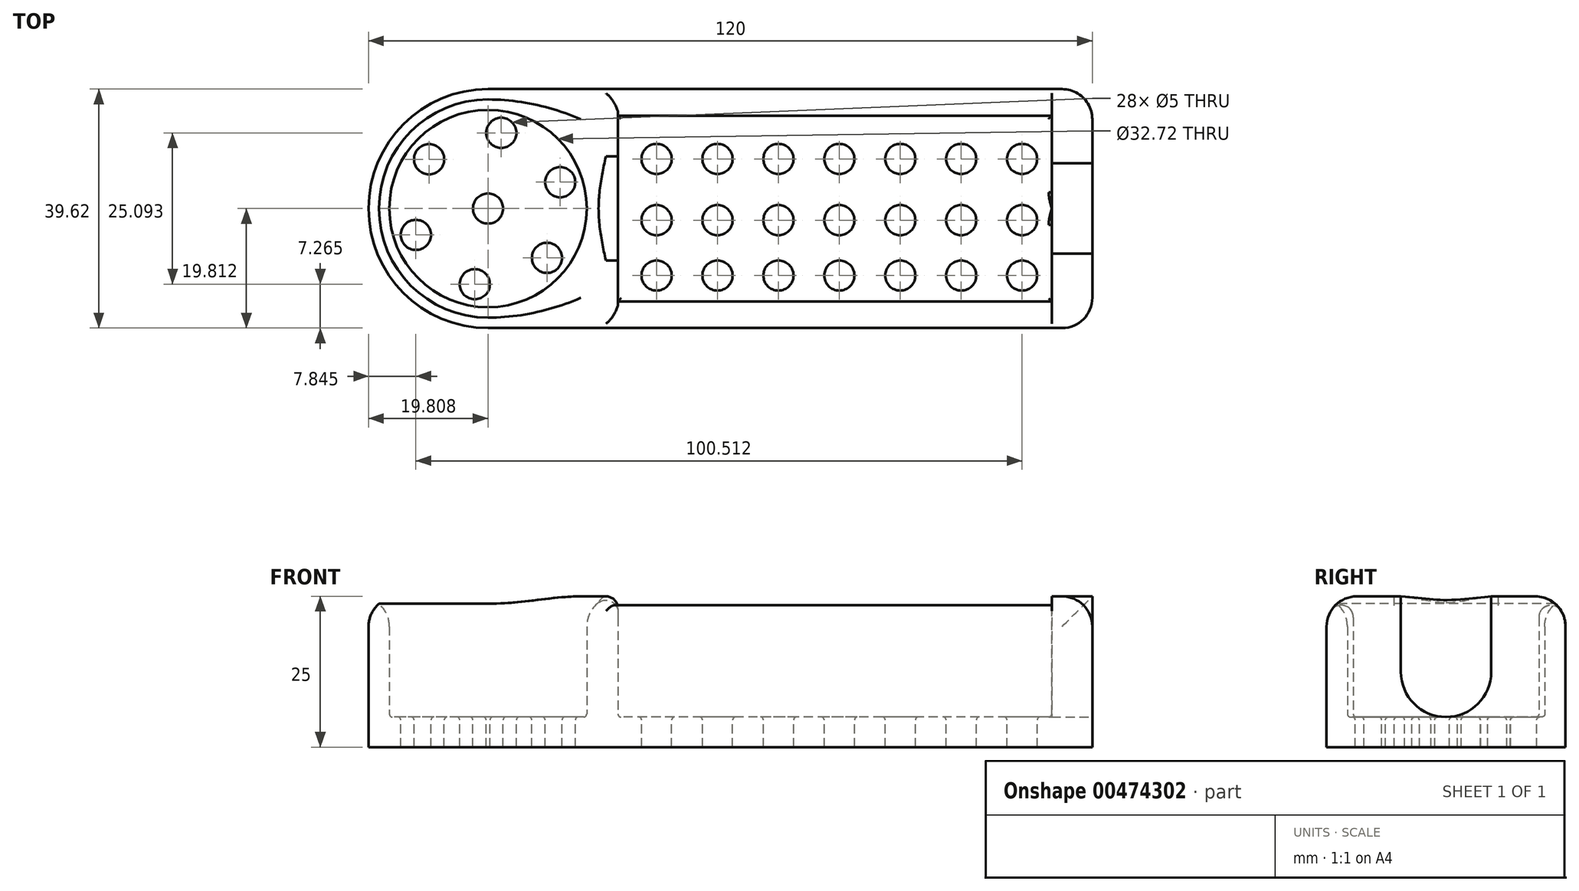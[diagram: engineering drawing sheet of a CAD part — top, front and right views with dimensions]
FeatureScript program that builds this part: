
annotation { "Feature Type Name" : "Feature", "Feature Type Description" : "" }
export const myFeature = defineFeature(function(context is Context, id is Id, definition is map)
    precondition{}
    {
        {
            var Q0;
            Q0=qCreatedBy(makeId("Top.planeOp"),FACE);
            var sketch = newSketch(context, id + "F0", { "sketchPlane" : qUnion([Q0])});
            skCircle(sketch, "E0", {"center": v(-57.21, 24.71) * mm, "radius": 19.8 * mm});
            skLineSegment(sketch, "E1", {"start": v(-57.21, 44.52) * mm, "end": v(42.98, 44.52) * mm});
            skLineSegment(sketch, "E2", {"start": v(42.98, 44.52) * mm, "end": v(42.98, 4.9) * mm});
            skLineSegment(sketch, "E3", {"start": v(42.98, 4.9) * mm, "end": v(-57.21, 4.9) * mm});
            skCircle(sketch, "E4", {"center": v(-57.21, 24.71) * mm, "radius": 16.36 * mm});
            skLineSegment(sketch, "E5.bottom", {"start": v(-35.67, 40.1) * mm, "end": v(36.25, 40.1) * mm});
            skLineSegment(sketch, "E5.top", {"start": v(-35.67, 9.33) * mm, "end": v(36.25, 9.33) * mm});
            skLineSegment(sketch, "E5.left", {"start": v(-35.67, 40.1) * mm, "end": v(-35.67, 9.33) * mm});
            skLineSegment(sketch, "E5.right", {"start": v(36.25, 40.1) * mm, "end": v(36.25, 9.33) * mm});
            skLineSegment(sketch, "E6", {"start": v(-35.67, 9.33) * mm, "end": v(-35.67, 4.9) * mm});
            skLineSegment(sketch, "E7", {"start": v(-35.67, 40.1) * mm, "end": v(-35.67, 44.52) * mm});
            skSolve(sketch);
        }
        {
            var Q0;
            Q0=makeQuery(id+"F0.imprint","IMPRINT",FACE,{"disambiguationData":[TD([[makeQuery(id+"F0.imprint","IMPRINT",EDGE,{"derivedFrom":sQuery(id+"F0.wireOp",EDGE,"E4")}),-1.0]])]});
            var Q1;
            Q1=makeQuery(id+"F0.imprint","IMPRINT",FACE,{"disambiguationData":[TD([[makeQuery(id+"F0.imprint","IMPRINT",EDGE,{"derivedFrom":sQuery(id+"F0.wireOp",EDGE,"E4")}),1.0]])]});
            var Q2;
            Q2=makeQuery(id+"F0.imprint","IMPRINT",FACE,{"disambiguationData":[TD([[makeQuery(id+"F0.imprint","IMPRINT",EDGE,{"derivedFrom":sQuery(id+"F0.wireOp",EDGE,"E5.left")}),-1.0]])]});
            var Q3;
            {var subQ1=sQuery(id+"F0.wireOp",EDGE,"E2");Q3=makeQuery(id+"F0.imprint","IMPRINT",FACE,{"disambiguationData":[TD([[makeQuery(id+"F0.imprint","IMPRINT",EDGE,{"derivedFrom":subQ1}),-1.0]])]});}
            var Q4;
            Q4=makeQuery(id+"F0.imprint","IMPRINT",FACE,{"disambiguationData":[TD([[makeQuery(id+"F0.imprint","IMPRINT",EDGE,{"derivedFrom":sQuery(id+"F0.wireOp",EDGE,"E5.bottom")}),-1.0]])]});
            extrude(context, id + "F1", {"entities" : qUnion([Q0, Q1, Q2, Q3, Q4]), "depth" : 5 * mm});
        }
        {
            var Q0;
            Q0=makeQuery(id+"F0.imprint","IMPRINT",FACE,{"disambiguationData":[TD([[makeQuery(id+"F0.imprint","IMPRINT",EDGE,{"derivedFrom":sQuery(id+"F0.wireOp",EDGE,"E4")}),-1.0]])]});
            var Q1;
            {var subQ1=sQuery(id+"F0.wireOp",EDGE,"E2");Q1=makeQuery(id+"F0.imprint","IMPRINT",FACE,{"disambiguationData":[TD([[makeQuery(id+"F0.imprint","IMPRINT",EDGE,{"derivedFrom":subQ1}),-1.0]])]});}
            var Q2;
            Q2=makeQuery(id+"F0.imprint","IMPRINT",FACE,{"disambiguationData":[TD([[makeQuery(id+"F0.imprint","IMPRINT",EDGE,{"derivedFrom":sQuery(id+"F0.wireOp",EDGE,"E5.left")}),-1.0]])]});
            extrude(context, id + "F2", {"entities" : qUnion([Q0, Q1, Q2]), "operationType" : NewBodyOperationType.ADD, "depth" : 25 * mm});
        }
        {
            var Q0;
            {var subQ0=sQuery(id+"F0.wireOp",EDGE,"E2");Q0=makeQuery(id+"F2.boolean.opBoolean","MERGE",FACE,{"derivedFrom":[makeQuery(id+"F1.opExtrude","SWEPT_FACE",FACE,{"disambiguationData":[OSD([subQ0])]}),makeQuery(id+"F2.opExtrude","SWEPT_FACE",FACE,{"disambiguationData":[OSD([subQ0])]})]});}
            var sketch = newSketch(context, id + "F3", { "sketchPlane" : qUnion([Q0])});
            skArc(sketch, "E8", {"start": v(17.21, 12.5) * mm, "mid": v(24.71, 5) * mm, "end": v(32.21, 12.5) * mm});
            skPoint(sketch, "E9.start.orphan", {"position": v(24.71, 25) * mm});
            skLineSegment(sketch, "E10", {"start": v(32.21, 12.5) * mm, "end": v(32.21, 25) * mm});
            skLineSegment(sketch, "E11", {"start": v(17.21, 12.5) * mm, "end": v(17.21, 25) * mm});
            skPoint(sketch, "E12.trimOffspring.end.orphan", {"position": v(24.71, 0) * mm});
            skSolve(sketch);
        }
        {
            var Q0;
            Q0=makeQuery(id+"F3.imprint","IMPRINT",FACE,{"disambiguationData":[TD([[makeQuery(id+"F3.imprint","IMPRINT",EDGE,{"derivedFrom":sQuery(id+"F3.wireOp",EDGE,"E8")}),1.0]])]});
            extrude(context, id + "F4", {"entities" : qUnion([Q0]), "operationType" : NewBodyOperationType.REMOVE, "oppositeDirection" : true, "depth" : 25 * mm});
        }
        {
            var Q0;
            Q0=makeQuery(id+"F4.boolean.opBoolean","COPY",EDGE,{"derivedFrom":makeQuery(id+"F4.opExtrude","SWEPT_EDGE",EDGE,{"disambiguationData":[OSD([sQuery(id+"F0.wireOp",EDGE,"E2"),sQuery(id+"F3.wireOp",EDGE,"E11")])]})});
            var Q1;
            Q1=makeQuery(id+"F4.boolean.opBoolean","COPY",EDGE,{"derivedFrom":makeQuery(id+"F4.opExtrude","SWEPT_EDGE",EDGE,{"disambiguationData":[OSD([sQuery(id+"F0.wireOp",EDGE,"E2"),sQuery(id+"F3.wireOp",EDGE,"E10")])]})});
            var Q2;
            Q2=makeQuery(id+"F4.boolean.opBoolean","COPY",EDGE,{"derivedFrom":makeQuery(id+"F4.opExtrude","CAP_EDGE",EDGE,{"disambiguationData":[OSD([sQuery(id+"F3.wireOp",EDGE,"E11")])],"isStart":true})});
            var Q3;
            {var subQ0=sQuery(id+"F0.wireOp",EDGE,"E3");var subQ1=sQuery(id+"F0.wireOp",EDGE,"E2");Q3=makeQuery(id+"F4.boolean.opBoolean","SPLIT",EDGE,{"disambiguationData":[TD([makeQuery(id+"F1.opExtrude","SWEPT_FACE",FACE,{"disambiguationData":[OSD([subQ0])]})])],"derivedFrom":makeQuery(id+"F2.opExtrude","CAP_EDGE",EDGE,{"disambiguationData":[OSD([subQ1])],"isStart":false})});}
            var Q4;
            Q4=makeQuery(id+"F2.opExtrude","CAP_EDGE",EDGE,{"disambiguationData":[OSD([sQuery(id+"F0.wireOp",EDGE,"E3")])],"isStart":false});
            var Q5;
            {var subQ0=sQuery(id+"F0.wireOp",EDGE,"E2");var subQ1=sQuery(id+"F0.wireOp",EDGE,"E1");Q5=makeQuery(id+"F2.boolean.opBoolean","MERGE",EDGE,{"derivedFrom":[makeQuery(id+"F1.opExtrude","SWEPT_EDGE",EDGE,{"disambiguationData":[OSD([subQ1,subQ0])]}),makeQuery(id+"F2.opExtrude","SWEPT_EDGE",EDGE,{"disambiguationData":[OSD([subQ1,subQ0])]})]});}
            var Q6;
            {var subQ0=sQuery(id+"F0.wireOp",EDGE,"E3");var subQ1=sQuery(id+"F0.wireOp",EDGE,"E2");Q6=makeQuery(id+"F2.boolean.opBoolean","MERGE",EDGE,{"derivedFrom":[makeQuery(id+"F1.opExtrude","SWEPT_EDGE",EDGE,{"disambiguationData":[OSD([subQ1,subQ0])]}),makeQuery(id+"F2.opExtrude","SWEPT_EDGE",EDGE,{"disambiguationData":[OSD([subQ1,subQ0])]})]});}
            var Q7;
            Q7=makeQuery(id+"F2.opExtrude","CAP_EDGE",EDGE,{"disambiguationData":[OSD([sQuery(id+"F0.wireOp",EDGE,"E4")])],"isStart":false});
            fillet(context, id + "F5", {"entities" : qUnion([Q0, Q1, Q2, Q3, Q4, Q5, Q6, Q7]), "radius" : 5 * mm, "tangentPropagation" : true, "allowEdgeOverflow" : false});
        }
        {
            var Q0;
            Q0=makeQuery(id+"F2.opExtrude","CAP_EDGE",EDGE,{"disambiguationData":[OSD([sQuery(id+"F0.wireOp",EDGE,"E5.left")])],"isStart":false});
            var Q1;
            Q1=makeQuery(id+"F5.opFillet","BLEND_EDGE",EDGE,{"blendedFrom":[makeQuery(id+"F2.opExtrude","CAP_EDGE",EDGE,{"disambiguationData":[OSD([sQuery(id+"F0.wireOp",EDGE,"E3")])],"isStart":false}),makeQuery(id+"F2.opExtrude","SWEPT_FACE",FACE,{"disambiguationData":[OSD([sQuery(id+"F0.wireOp",EDGE,"E5.top")])]})],"blendedInto":[makeQuery(id+"F2.opExtrude","SWEPT_FACE",FACE,{"disambiguationData":[OSD([sQuery(id+"F0.wireOp",EDGE,"E5.top")])]})]});
            var Q2;
            Q2=makeQuery(id+"F5.opFillet","BLEND_EDGE",EDGE,{"blendedFrom":[makeQuery(id+"F2.opExtrude","CAP_EDGE",EDGE,{"disambiguationData":[OSD([sQuery(id+"F0.wireOp",EDGE,"E1")])],"isStart":false}),makeQuery(id+"F2.opExtrude","SWEPT_FACE",FACE,{"disambiguationData":[OSD([sQuery(id+"F0.wireOp",EDGE,"E5.bottom")])]})],"blendedInto":[makeQuery(id+"F2.opExtrude","SWEPT_FACE",FACE,{"disambiguationData":[OSD([sQuery(id+"F0.wireOp",EDGE,"E5.bottom")])]})]});
            var Q3;
            {var subQ0=sQuery(id+"F0.wireOp",EDGE,"E5.right");var subQ1=makeQuery(id+"F2.opExtrude","SWEPT_FACE",FACE,{"disambiguationData":[OSD([subQ0])]});var subQ2=sQuery(id+"F0.wireOp",EDGE,"E5.bottom");var subQ4=sQuery(id+"F0.wireOp",EDGE,"E2");var subQ7=sQuery(id+"F3.wireOp",EDGE,"E10");Q3=makeQuery(id+"F5.opFillet","BLEND_EDGE",EDGE,{"blendedFrom":[makeQuery(id+"F4.boolean.opBoolean","COPY",EDGE,{"derivedFrom":makeQuery(id+"F4.opExtrude","SWEPT_EDGE",EDGE,{"disambiguationData":[OSD([subQ4,subQ7])]})}),makeQuery(id+"F4.boolean.opBoolean","SPLIT",FACE,{"disambiguationData":[TD([makeQuery(id+"F2.opExtrude","SWEPT_FACE",FACE,{"disambiguationData":[OSD([subQ2])]})])],"derivedFrom":subQ1})],"blendedInto":[makeQuery(id+"F4.boolean.opBoolean","SPLIT",FACE,{"disambiguationData":[TD([makeQuery(id+"F2.opExtrude","SWEPT_FACE",FACE,{"disambiguationData":[OSD([subQ2])]})])],"derivedFrom":subQ1})]});}
            fillet(context, id + "F6", {"entities" : qUnion([Q0, Q1, Q2, Q3]), "radius" : 2 * mm, "tangentPropagation" : true, "allowEdgeOverflow" : false});
        }
        {
            var Q0;
            Q0=makeQuery(id+"F2.boolean.opBoolean","SPLIT",FACE,{"disambiguationData":[TD([makeQuery(id+"F2.opExtrude","SWEPT_FACE",FACE,{"disambiguationData":[OSD([sQuery(id+"F0.wireOp",EDGE,"E5.bottom")])]})])],"derivedFrom":makeQuery(id+"F1.opExtrude","CAP_FACE",FACE,{"disambiguationData":[OSD([sQuery(id+"F0.wireOp",EDGE,"E0"),sQuery(id+"F0.wireOp",EDGE,"E1"),sQuery(id+"F0.wireOp",EDGE,"E2"),sQuery(id+"F0.wireOp",EDGE,"E3")])],"isStart":false})});
            var sketch = newSketch(context, id + "F7", { "sketchPlane" : qUnion([Q0])});
            skCircle(sketch, "E13", {"center": v(-29.26, 32.94) * mm, "radius": 2.5 * mm});
            skCircle(sketch, "E14.1.0.0", {"center": v(-19.16, 32.94) * mm, "radius": 2.5 * mm});
            skCircle(sketch, "E14.2.0.0", {"center": v(-9.06, 32.94) * mm, "radius": 2.5 * mm});
            skCircle(sketch, "E14.3.0.0", {"center": v(1.04, 32.94) * mm, "radius": 2.5 * mm});
            skCircle(sketch, "E14.4.0.0", {"center": v(11.14, 32.94) * mm, "radius": 2.5 * mm});
            skCircle(sketch, "E14.5.0.0", {"center": v(21.24, 32.94) * mm, "radius": 2.5 * mm});
            skCircle(sketch, "E14.6.0.0", {"center": v(31.34, 32.94) * mm, "radius": 2.5 * mm});
            skLineSegment(sketch, "E14.direction1", {"start": v(-29.26, 32.94) * mm, "end": v(-19.16, 32.94) * mm, "construction": true});
            skCircle(sketch, "E15", {"center": v(-29.26, 22.78) * mm, "radius": 2.5 * mm});
            skCircle(sketch, "E16.1.0.0", {"center": v(-19.16, 22.78) * mm, "radius": 2.5 * mm});
            skCircle(sketch, "E16.2.0.0", {"center": v(-9.06, 22.78) * mm, "radius": 2.5 * mm});
            skCircle(sketch, "E16.3.0.0", {"center": v(1.04, 22.78) * mm, "radius": 2.5 * mm});
            skCircle(sketch, "E16.4.0.0", {"center": v(11.14, 22.78) * mm, "radius": 2.5 * mm});
            skCircle(sketch, "E16.5.0.0", {"center": v(21.24, 22.78) * mm, "radius": 2.5 * mm});
            skCircle(sketch, "E16.6.0.0", {"center": v(31.34, 22.78) * mm, "radius": 2.5 * mm});
            skLineSegment(sketch, "E16.direction1", {"start": v(-29.26, 22.78) * mm, "end": v(-19.16, 22.78) * mm, "construction": true});
            skCircle(sketch, "E17", {"center": v(-29.26, 13.6) * mm, "radius": 2.5 * mm});
            skCircle(sketch, "E18.1.0.0", {"center": v(-19.16, 13.6) * mm, "radius": 2.5 * mm});
            skCircle(sketch, "E18.2.0.0", {"center": v(-9.06, 13.6) * mm, "radius": 2.5 * mm});
            skCircle(sketch, "E18.3.0.0", {"center": v(1.04, 13.6) * mm, "radius": 2.5 * mm});
            skCircle(sketch, "E18.4.0.0", {"center": v(11.14, 13.6) * mm, "radius": 2.5 * mm});
            skCircle(sketch, "E18.5.0.0", {"center": v(21.24, 13.6) * mm, "radius": 2.5 * mm});
            skCircle(sketch, "E18.6.0.0", {"center": v(31.34, 13.6) * mm, "radius": 2.5 * mm});
            skLineSegment(sketch, "E18.direction1", {"start": v(-29.26, 13.6) * mm, "end": v(-19.16, 13.6) * mm, "construction": true});
            skSolve(sketch);
        }
        {
            var Q0;
            Q0=makeQuery(id+"F7.imprint","IMPRINT",FACE,{"disambiguationData":[TD([[makeQuery(id+"F7.imprint","IMPRINT",EDGE,{"derivedFrom":sQuery(id+"F7.wireOp",EDGE,"E13")}),1.0]])]});
            var Q1;
            Q1=makeQuery(id+"F7.imprint","IMPRINT",FACE,{"disambiguationData":[TD([[makeQuery(id+"F7.imprint","IMPRINT",EDGE,{"derivedFrom":sQuery(id+"F7.wireOp",EDGE,"E14.1.0.0")}),1.0]])]});
            var Q2;
            Q2=makeQuery(id+"F7.imprint","IMPRINT",FACE,{"disambiguationData":[TD([[makeQuery(id+"F7.imprint","IMPRINT",EDGE,{"derivedFrom":sQuery(id+"F7.wireOp",EDGE,"E14.2.0.0")}),1.0]])]});
            var Q3;
            Q3=makeQuery(id+"F7.imprint","IMPRINT",FACE,{"disambiguationData":[TD([[makeQuery(id+"F7.imprint","IMPRINT",EDGE,{"derivedFrom":sQuery(id+"F7.wireOp",EDGE,"E14.3.0.0")}),1.0]])]});
            var Q4;
            Q4=makeQuery(id+"F7.imprint","IMPRINT",FACE,{"disambiguationData":[TD([[makeQuery(id+"F7.imprint","IMPRINT",EDGE,{"derivedFrom":sQuery(id+"F7.wireOp",EDGE,"E14.4.0.0")}),1.0]])]});
            var Q5;
            Q5=makeQuery(id+"F7.imprint","IMPRINT",FACE,{"disambiguationData":[TD([[makeQuery(id+"F7.imprint","IMPRINT",EDGE,{"derivedFrom":sQuery(id+"F7.wireOp",EDGE,"E14.5.0.0")}),1.0]])]});
            var Q6;
            Q6=makeQuery(id+"F7.imprint","IMPRINT",FACE,{"disambiguationData":[TD([[makeQuery(id+"F7.imprint","IMPRINT",EDGE,{"derivedFrom":sQuery(id+"F7.wireOp",EDGE,"E14.6.0.0")}),1.0]])]});
            var Q7;
            Q7=makeQuery(id+"F7.imprint","IMPRINT",FACE,{"disambiguationData":[TD([[makeQuery(id+"F7.imprint","IMPRINT",EDGE,{"derivedFrom":sQuery(id+"F7.wireOp",EDGE,"E16.6.0.0")}),1.0]])]});
            var Q8;
            Q8=makeQuery(id+"F7.imprint","IMPRINT",FACE,{"disambiguationData":[TD([[makeQuery(id+"F7.imprint","IMPRINT",EDGE,{"derivedFrom":sQuery(id+"F7.wireOp",EDGE,"E18.6.0.0")}),1.0]])]});
            var Q9;
            Q9=makeQuery(id+"F7.imprint","IMPRINT",FACE,{"disambiguationData":[TD([[makeQuery(id+"F7.imprint","IMPRINT",EDGE,{"derivedFrom":sQuery(id+"F7.wireOp",EDGE,"E18.5.0.0")}),1.0]])]});
            var Q10;
            Q10=makeQuery(id+"F7.imprint","IMPRINT",FACE,{"disambiguationData":[TD([[makeQuery(id+"F7.imprint","IMPRINT",EDGE,{"derivedFrom":sQuery(id+"F7.wireOp",EDGE,"E16.5.0.0")}),1.0]])]});
            var Q11;
            Q11=makeQuery(id+"F7.imprint","IMPRINT",FACE,{"disambiguationData":[TD([[makeQuery(id+"F7.imprint","IMPRINT",EDGE,{"derivedFrom":sQuery(id+"F7.wireOp",EDGE,"E16.4.0.0")}),1.0]])]});
            var Q12;
            Q12=makeQuery(id+"F7.imprint","IMPRINT",FACE,{"disambiguationData":[TD([[makeQuery(id+"F7.imprint","IMPRINT",EDGE,{"derivedFrom":sQuery(id+"F7.wireOp",EDGE,"E18.4.0.0")}),1.0]])]});
            var Q13;
            Q13=makeQuery(id+"F7.imprint","IMPRINT",FACE,{"disambiguationData":[TD([[makeQuery(id+"F7.imprint","IMPRINT",EDGE,{"derivedFrom":sQuery(id+"F7.wireOp",EDGE,"E18.3.0.0")}),1.0]])]});
            var Q14;
            Q14=makeQuery(id+"F7.imprint","IMPRINT",FACE,{"disambiguationData":[TD([[makeQuery(id+"F7.imprint","IMPRINT",EDGE,{"derivedFrom":sQuery(id+"F7.wireOp",EDGE,"E16.3.0.0")}),1.0]])]});
            var Q15;
            Q15=makeQuery(id+"F7.imprint","IMPRINT",FACE,{"disambiguationData":[TD([[makeQuery(id+"F7.imprint","IMPRINT",EDGE,{"derivedFrom":sQuery(id+"F7.wireOp",EDGE,"E16.2.0.0")}),1.0]])]});
            var Q16;
            Q16=makeQuery(id+"F7.imprint","IMPRINT",FACE,{"disambiguationData":[TD([[makeQuery(id+"F7.imprint","IMPRINT",EDGE,{"derivedFrom":sQuery(id+"F7.wireOp",EDGE,"E18.2.0.0")}),1.0]])]});
            var Q17;
            Q17=makeQuery(id+"F7.imprint","IMPRINT",FACE,{"disambiguationData":[TD([[makeQuery(id+"F7.imprint","IMPRINT",EDGE,{"derivedFrom":sQuery(id+"F7.wireOp",EDGE,"E18.1.0.0")}),1.0]])]});
            var Q18;
            Q18=makeQuery(id+"F7.imprint","IMPRINT",FACE,{"disambiguationData":[TD([[makeQuery(id+"F7.imprint","IMPRINT",EDGE,{"derivedFrom":sQuery(id+"F7.wireOp",EDGE,"E16.1.0.0")}),1.0]])]});
            var Q19;
            Q19=makeQuery(id+"F7.imprint","IMPRINT",FACE,{"disambiguationData":[TD([[makeQuery(id+"F7.imprint","IMPRINT",EDGE,{"derivedFrom":sQuery(id+"F7.wireOp",EDGE,"E15")}),1.0]])]});
            var Q20;
            Q20=makeQuery(id+"F7.imprint","IMPRINT",FACE,{"disambiguationData":[TD([[makeQuery(id+"F7.imprint","IMPRINT",EDGE,{"derivedFrom":sQuery(id+"F7.wireOp",EDGE,"E17")}),1.0]])]});
            extrude(context, id + "F8", {"entities" : qUnion([Q0, Q1, Q2, Q3, Q4, Q5, Q6, Q7, Q8, Q9, Q10, Q11, Q12, Q13, Q14, Q15, Q16, Q17, Q18, Q19, Q20]), "operationType" : NewBodyOperationType.REMOVE, "oppositeDirection" : true, "depth" : 25 * mm});
        }
        {
            var Q0;
            Q0=makeQuery(id+"F2.boolean.opBoolean","SPLIT",FACE,{"disambiguationData":[TD([makeQuery(id+"F2.opExtrude","SWEPT_FACE",FACE,{"disambiguationData":[OSD([sQuery(id+"F0.wireOp",EDGE,"E4")])]})])],"derivedFrom":makeQuery(id+"F1.opExtrude","CAP_FACE",FACE,{"disambiguationData":[OSD([sQuery(id+"F0.wireOp",EDGE,"E0"),sQuery(id+"F0.wireOp",EDGE,"E1"),sQuery(id+"F0.wireOp",EDGE,"E2"),sQuery(id+"F0.wireOp",EDGE,"E3")])],"isStart":false})});
            var sketch = newSketch(context, id + "F9", { "sketchPlane" : qUnion([Q0])});
            skCircle(sketch, "E19", {"center": v(-55.02, 37.26) * mm, "radius": 2.5 * mm});
            skCircle(sketch, "E20.1.0", {"center": v(-66.98, 32.89) * mm, "radius": 2.5 * mm});
            skCircle(sketch, "E20.2.0", {"center": v(-69.17, 20.34) * mm, "radius": 2.5 * mm});
            skCircle(sketch, "E20.3.0", {"center": v(-59.4, 12.16) * mm, "radius": 2.5 * mm});
            skCircle(sketch, "E20.4.0", {"center": v(-47.44, 16.54) * mm, "radius": 2.5 * mm});
            skCircle(sketch, "E20.5.0", {"center": v(-45.25, 29.08) * mm, "radius": 2.5 * mm});
            skPoint(sketch, "E20.center", {"position": v(-57.21, 24.71) * mm});
            skCircle(sketch, "E21", {"center": v(-57.21, 24.71) * mm, "radius": 2.5 * mm});
            skSolve(sketch);
        }
        {
            var Q0;
            Q0=makeQuery(id+"F9.imprint","IMPRINT",FACE,{"disambiguationData":[TD([[makeQuery(id+"F9.imprint","IMPRINT",EDGE,{"derivedFrom":sQuery(id+"F9.wireOp",EDGE,"E19")}),1.0]])]});
            var Q1;
            Q1=makeQuery(id+"F9.imprint","IMPRINT",FACE,{"disambiguationData":[TD([[makeQuery(id+"F9.imprint","IMPRINT",EDGE,{"derivedFrom":sQuery(id+"F9.wireOp",EDGE,"E20.1.0")}),1.0]])]});
            var Q2;
            Q2=makeQuery(id+"F9.imprint","IMPRINT",FACE,{"disambiguationData":[TD([[makeQuery(id+"F9.imprint","IMPRINT",EDGE,{"derivedFrom":sQuery(id+"F9.wireOp",EDGE,"E21")}),1.0]])]});
            var Q3;
            Q3=makeQuery(id+"F9.imprint","IMPRINT",FACE,{"disambiguationData":[TD([[makeQuery(id+"F9.imprint","IMPRINT",EDGE,{"derivedFrom":sQuery(id+"F9.wireOp",EDGE,"E20.2.0")}),1.0]])]});
            var Q4;
            Q4=makeQuery(id+"F9.imprint","IMPRINT",FACE,{"disambiguationData":[TD([[makeQuery(id+"F9.imprint","IMPRINT",EDGE,{"derivedFrom":sQuery(id+"F9.wireOp",EDGE,"E20.3.0")}),1.0]])]});
            var Q5;
            Q5=makeQuery(id+"F9.imprint","IMPRINT",FACE,{"disambiguationData":[TD([[makeQuery(id+"F9.imprint","IMPRINT",EDGE,{"derivedFrom":sQuery(id+"F9.wireOp",EDGE,"E20.4.0")}),1.0]])]});
            var Q6;
            Q6=makeQuery(id+"F9.imprint","IMPRINT",FACE,{"disambiguationData":[TD([[makeQuery(id+"F9.imprint","IMPRINT",EDGE,{"derivedFrom":sQuery(id+"F9.wireOp",EDGE,"E20.5.0")}),1.0]])]});
            extrude(context, id + "F10", {"entities" : qUnion([Q0, Q1, Q2, Q3, Q4, Q5, Q6]), "operationType" : NewBodyOperationType.REMOVE, "oppositeDirection" : true, "depth" : 25 * mm});
        }
        {
            var Q0;
            Q0=makeQuery(id+"F8.boolean.opBoolean","COPY",EDGE,{"derivedFrom":makeQuery(id+"F8.opExtrude","CAP_EDGE",EDGE,{"disambiguationData":[OSD([sQuery(id+"F7.wireOp",EDGE,"E14.1.0.0")])],"isStart":true})});
            var Q1;
            Q1=makeQuery(id+"F8.boolean.opBoolean","COPY",EDGE,{"derivedFrom":makeQuery(id+"F8.opExtrude","CAP_EDGE",EDGE,{"disambiguationData":[OSD([sQuery(id+"F7.wireOp",EDGE,"E14.2.0.0")])],"isStart":true})});
            var Q2;
            Q2=makeQuery(id+"F2.boolean.opBoolean","SPLIT",FACE,{"disambiguationData":[TD([makeQuery(id+"F2.opExtrude","SWEPT_FACE",FACE,{"disambiguationData":[OSD([sQuery(id+"F0.wireOp",EDGE,"E5.bottom")])]})])],"derivedFrom":makeQuery(id+"F1.opExtrude","CAP_FACE",FACE,{"disambiguationData":[OSD([sQuery(id+"F0.wireOp",EDGE,"E0"),sQuery(id+"F0.wireOp",EDGE,"E1"),sQuery(id+"F0.wireOp",EDGE,"E2"),sQuery(id+"F0.wireOp",EDGE,"E3")])],"isStart":false})});
            fillet(context, id + "F11", {"entities" : qUnion([Q0, Q1, Q2]), "radius" : .5 * mm, "tangentPropagation" : true, "allowEdgeOverflow" : false});
        }
        {
            var Q0;
            Q0=makeQuery(id+"F2.boolean.opBoolean","SPLIT",FACE,{"disambiguationData":[TD([makeQuery(id+"F2.opExtrude","SWEPT_FACE",FACE,{"disambiguationData":[OSD([sQuery(id+"F0.wireOp",EDGE,"E4")])]})])],"derivedFrom":makeQuery(id+"F1.opExtrude","CAP_FACE",FACE,{"disambiguationData":[OSD([sQuery(id+"F0.wireOp",EDGE,"E0"),sQuery(id+"F0.wireOp",EDGE,"E1"),sQuery(id+"F0.wireOp",EDGE,"E2"),sQuery(id+"F0.wireOp",EDGE,"E3")])],"isStart":false})});
            fillet(context, id + "F12", {"entities" : qUnion([Q0]), "radius" : .5 * mm, "tangentPropagation" : true, "allowEdgeOverflow" : false});
        }
    });
